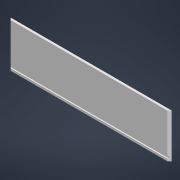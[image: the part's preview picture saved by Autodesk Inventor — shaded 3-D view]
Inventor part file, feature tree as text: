
AUTODESK INVENTOR PART (.ipt)
format: ipt  version: 2022 (Build 260153000, 153)  size: 105,472 bytes
history: native  units: in
note: dims shown in document units (in); Inventor stores cm internally (conversion verified against a paired STEP export)
features: extrude x2, chamfer x2, sketch x2
ambient origin geometry x8: Origin, YZ Plane, XZ Plane, XY Plane, X Axis, Y Axis, Z Axis, Center Point
bodies: Solid1 (feature_tree)
feature tree (6):
  extrude  "Extrusion1"  Depth=2.3622in
  extrude  "Extrusion2"  Depth=0.1181in
  chamfer  "Chamfer1"  Angle=90.0deg  [1 undecoded]
  chamfer  "Chamfer2"  Distance=8.6614in
  sketch  "Sketch1"  dims[d0=8.6614in d1=2.3622in]
  sketch  "Sketch2"  dims[d2=0.1181in d3=0.0in d4=0.1181in d5=90.0deg d6=8.6614in d7=0.1181in d8=0.0591in d9=0.0in d10=0.1181in d11=0.0787in d12=45.0deg d13=0.1181in d14=0.0787in d15=45.0deg]
note: 1 required parameter value undecoded (feature->parameter linkage not recoverable at this tier; creation-order binding heuristic only, values carry confidence <= 0.55)
